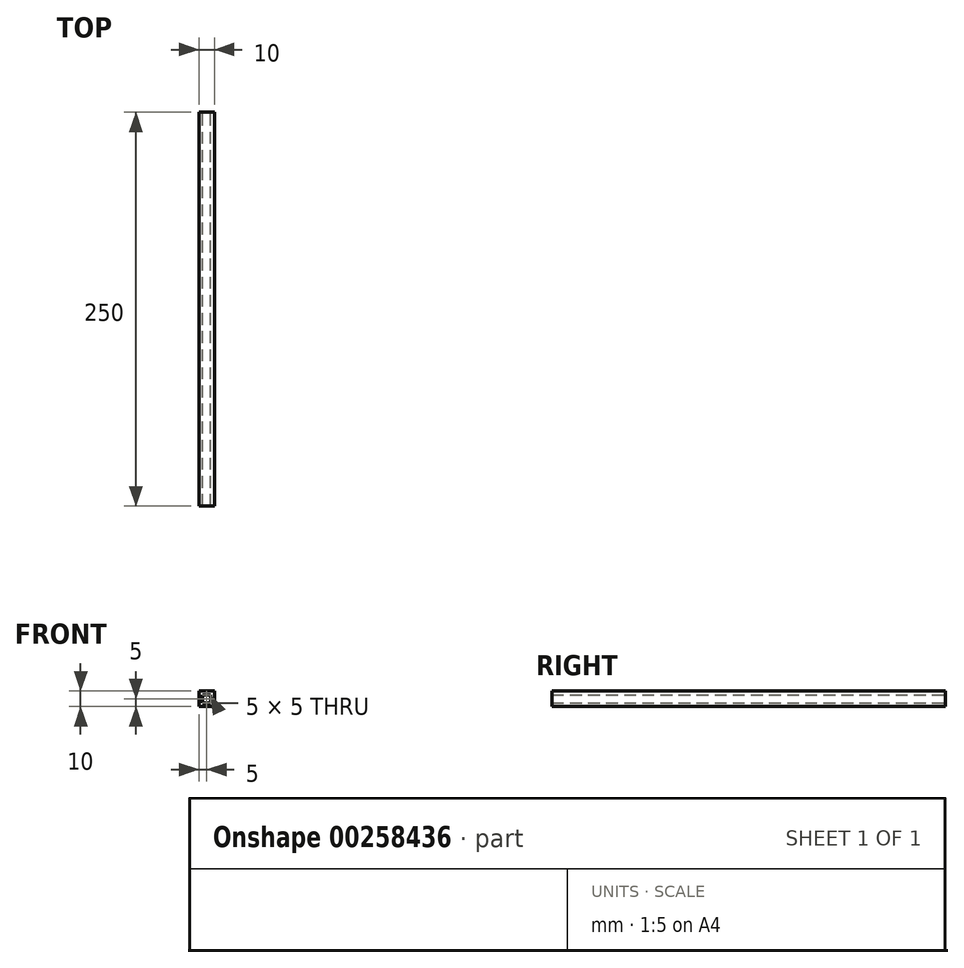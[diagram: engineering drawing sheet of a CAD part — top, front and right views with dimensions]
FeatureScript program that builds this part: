
annotation { "Feature Type Name" : "Feature", "Feature Type Description" : "" }
export const myFeature = defineFeature(function(context is Context, id is Id, definition is map)
    precondition{}
    {
        {
            var Q0;
            Q0=qCreatedBy(makeId("Front.planeOp"),FACE);
            var sketch = newSketch(context, id + "F0", { "sketchPlane" : qUnion([Q0])});
            skLineSegment(sketch, "E0.bottom", {"start": v(5, -5) * mm, "end": v(-5, -5) * mm});
            skLineSegment(sketch, "E0.top", {"start": v(5, 5) * mm, "end": v(-5, 5) * mm});
            skLineSegment(sketch, "E0.left", {"start": v(5, -5) * mm, "end": v(5, 5) * mm});
            skLineSegment(sketch, "E0.right", {"start": v(-5, -5) * mm, "end": v(-5, 5) * mm});
            skPoint(sketch, "E0.middle", {"position": v(0, 0) * mm});
            skLineSegment(sketch, "E1.bottom", {"start": v(2.5, -2.5) * mm, "end": v(-2.5, -2.5) * mm});
            skLineSegment(sketch, "E1.top", {"start": v(2.5, 2.5) * mm, "end": v(-2.5, 2.5) * mm});
            skLineSegment(sketch, "E1.left", {"start": v(2.5, -2.5) * mm, "end": v(2.5, 2.5) * mm});
            skLineSegment(sketch, "E1.right", {"start": v(-2.5, -2.5) * mm, "end": v(-2.5, 2.5) * mm});
            skSolve(sketch);
        }
        {
            var Q0;
            Q0=makeQuery(id+"F0.imprint","IMPRINT",FACE,{"disambiguationData":[TD([[makeQuery(id+"F0.imprint","IMPRINT",EDGE,{"derivedFrom":sQuery(id+"F0.wireOp",EDGE,"E0.bottom")}),-1.0]])]});
            extrude(context, id + "F1", {"entities" : qUnion([Q0]), "depth" : 250 * mm});
        }
    });
